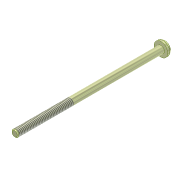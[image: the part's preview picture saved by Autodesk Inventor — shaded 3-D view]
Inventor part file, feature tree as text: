
AUTODESK INVENTOR PART (.ipt)
format: ipt  version: 2016 SP1 (Build 200210100, 210)  size: 104,960 bytes
history: native  units: mm
features: imported_body x1, thread x1
ambient origin geometry x8: Origin, YZ Plane, XZ Plane, XY Plane, X Axis, Y Axis, Z Axis, Center Point
bodies: Solid1 (feature_tree)
feature tree (2):
  imported_body  "Base1"
  thread  "Thread1"  [1 undecoded]
note: 1 required parameter value undecoded (feature->parameter linkage not recoverable at this tier; creation-order binding heuristic only, values carry confidence <= 0.55)
